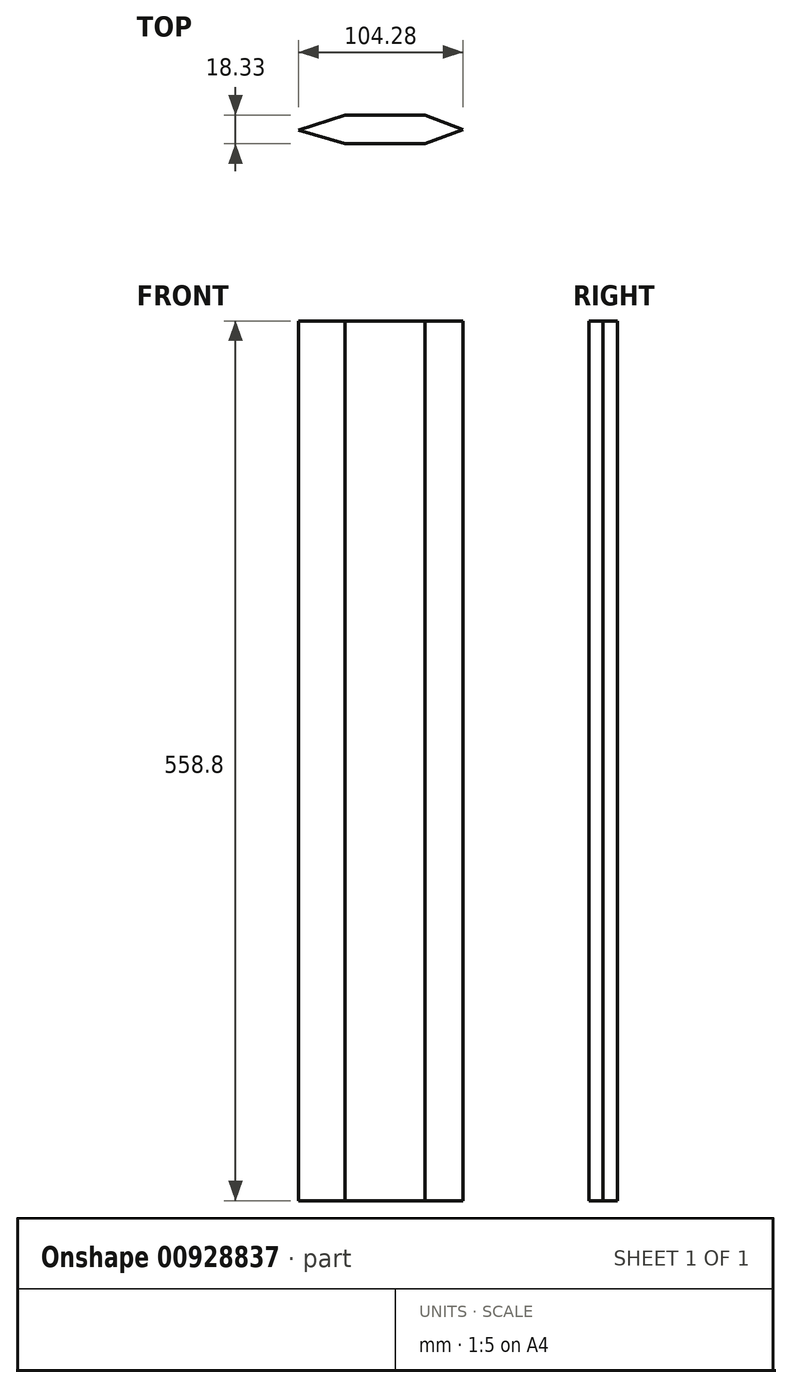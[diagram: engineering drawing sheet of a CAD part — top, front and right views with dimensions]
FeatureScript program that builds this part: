
annotation { "Feature Type Name" : "Feature", "Feature Type Description" : "" }
export const myFeature = defineFeature(function(context is Context, id is Id, definition is map)
    precondition{}
    {
        {
            var Q0;
            Q0=qCreatedBy(makeId("Top.planeOp"),FACE);
            var sketch = newSketch(context, id + "F0", { "sketchPlane" : qUnion([Q0])});
            skLineSegment(sketch, "E0", {"start": v(0, 0) * mm, "end": v(50.8, 0) * mm});
            skLineSegment(sketch, "E1", {"start": v(50.8, 0) * mm, "end": v(74.9, -9.43) * mm});
            skLineSegment(sketch, "E2", {"start": v(74.9, -9.43) * mm, "end": v(50.8, -18.33) * mm});
            skLineSegment(sketch, "E3", {"start": v(50.8, -18.33) * mm, "end": v(0, -18.33) * mm});
            skLineSegment(sketch, "E4", {"start": v(0, -18.33) * mm, "end": v(-29.4, -9.69) * mm});
            skLineSegment(sketch, "E5", {"start": v(-29.4, -9.69) * mm, "end": v(0, 0) * mm});
            skSolve(sketch);
        }
        {
            var Q0;
            Q0=makeQuery(id+"F0.imprint","IMPRINT",FACE,{"disambiguationData":[TD([[makeQuery(id+"F0.imprint","IMPRINT",EDGE,{"derivedFrom":sQuery(id+"F0.wireOp",EDGE,"E0")}),-1.0]])]});
            extrude(context, id + "F1", {"entities" : qUnion([Q0]), "depth" : 558.8 * mm, "offsetDistance" : 25.4 * mm});
        }
    });
